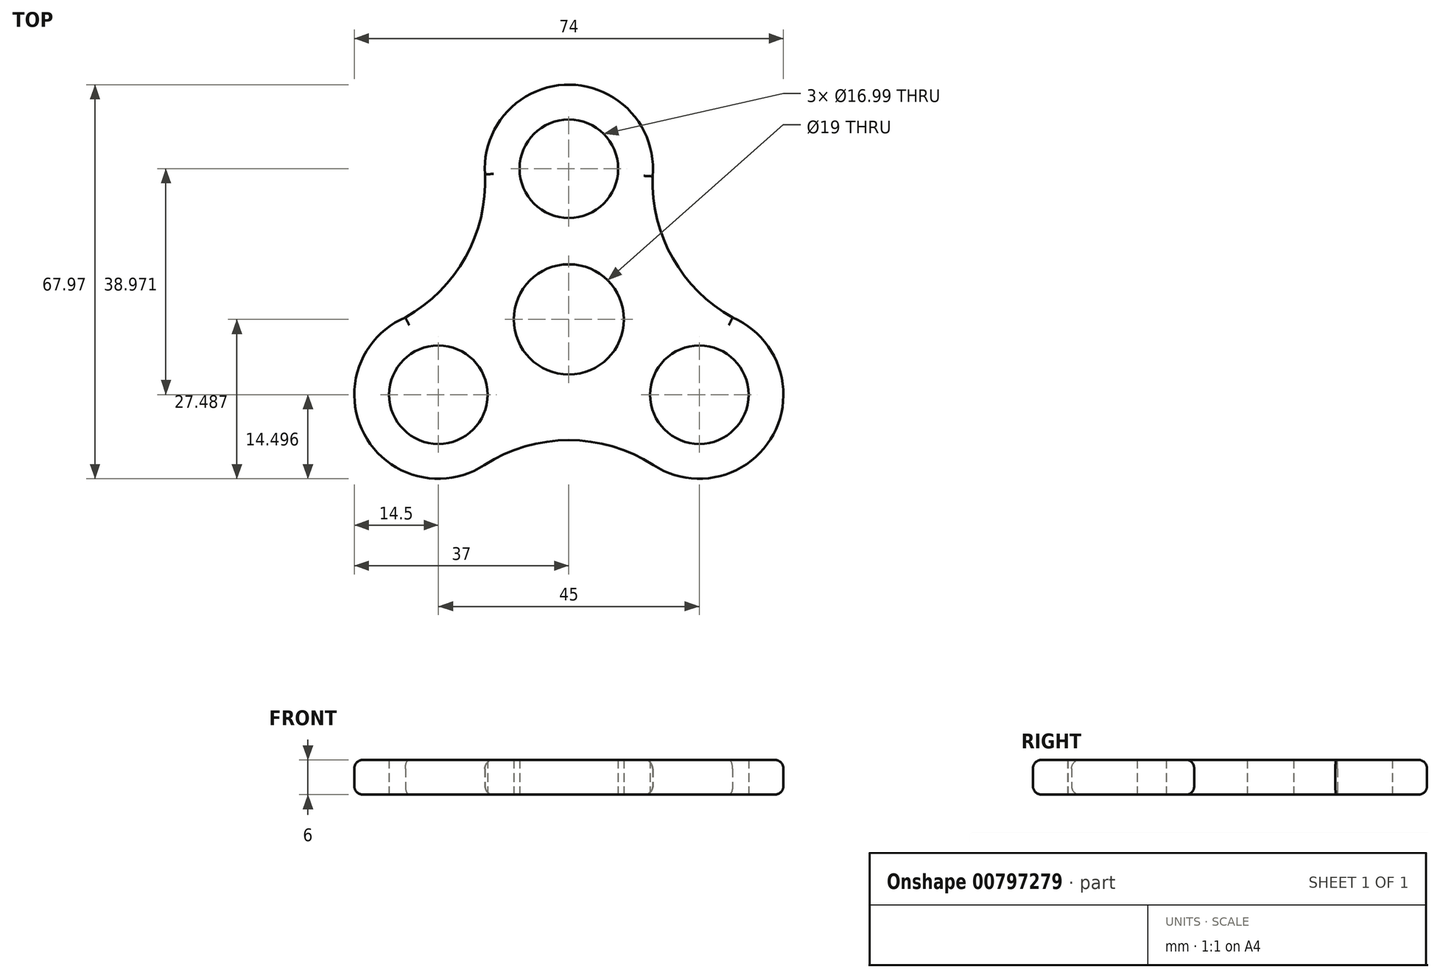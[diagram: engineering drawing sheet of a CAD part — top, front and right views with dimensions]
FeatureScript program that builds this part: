
annotation { "Feature Type Name" : "Feature", "Feature Type Description" : "" }
export const myFeature = defineFeature(function(context is Context, id is Id, definition is map)
    precondition{}
    {
        {
            var Q0;
            Q0=qCreatedBy(makeId("Top.planeOp"),FACE);
            var sketch = newSketch(context, id + "F0", { "sketchPlane" : qUnion([Q0])});
            skLineSegment(sketch, "E0", {"start": v(0, 26.77) * mm, "end": v(-22.5, -12.2) * mm, "construction": true});
            skLineSegment(sketch, "E1", {"start": v(-22.5, -12.2) * mm, "end": v(22.5, -12.2) * mm, "construction": true});
            skLineSegment(sketch, "E2", {"start": v(22.5, -12.2) * mm, "end": v(0, 26.77) * mm, "construction": true});
            skArc(sketch, "E3.0", {"start": v(-14.49, 26.16) * mm, "mid": v(-18.18, 10.92) * mm, "end": v(-29.75, 0.33) * mm});
            skArc(sketch, "E4.0", {"start": v(14.44, 25.45) * mm, "mid": v(0.17, 41.27) * mm, "end": v(-14.47, 25.8) * mm});
            skArc(sketch, "E5.0", {"start": v(28.46, 1) * mm, "mid": v(17.95, 11.3) * mm, "end": v(14.44, 25.6) * mm});
            skArc(sketch, "E6.0", {"start": v(14.57, -24.35) * mm, "mid": v(35.27, -19.06) * mm, "end": v(28.24, 1.1) * mm});
            skArc(sketch, "E7.0", {"start": v(-28.2, 1.13) * mm, "mid": v(-35.29, -19.04) * mm, "end": v(-14.57, -24.35) * mm});
            skArc(sketch, "E8.0", {"start": v(-14.64, -24.39) * mm, "mid": v(-0.03, -20.05) * mm, "end": v(14.58, -24.35) * mm});
            skLineSegment(sketch, "E9", {"start": v(-11.25, 7.28) * mm, "end": v(22.5, -12.2) * mm, "construction": true});
            skLineSegment(sketch, "E10", {"start": v(11.25, 7.28) * mm, "end": v(-22.5, -12.2) * mm, "construction": true});
            skLineSegment(sketch, "E11", {"start": v(0, -12.2) * mm, "end": v(0, 26.77) * mm, "construction": true});
            skCircle(sketch, "E12", {"center": v(22.5, -12.2) * mm, "radius": 8.5 * mm});
            skCircle(sketch, "E13", {"center": v(-22.5, -12.2) * mm, "radius": 8.5 * mm});
            skCircle(sketch, "E14", {"center": v(0, 26.77) * mm, "radius": 8.5 * mm});
            skCircle(sketch, "E15", {"center": v(0, 0.79) * mm, "radius": 9.5 * mm});
            skSolve(sketch);
        }
        {
            var Q0;
            Q0 = qSketchRegion(id + "F0", true);
            extrude(context, id + "F1", {"entities" : qUnion([Q0]), "depth" : 6 * mm, "offsetDistance" : 25.4 * mm});
        }
        {
            var Q0;
            Q0=makeQuery(id+"F1.opExtrude","CAP_EDGE",EDGE,{"disambiguationData":[OSD([sQuery(id+"F0.wireOp",EDGE,"E5.0")])],"isStart":false});
            var Q1;
            Q1=makeQuery(id+"F1.opExtrude","CAP_EDGE",EDGE,{"disambiguationData":[OSD([sQuery(id+"F0.wireOp",EDGE,"E3.0")])],"isStart":false});
            var Q2;
            Q2=makeQuery(id+"F1.opExtrude","CAP_EDGE",EDGE,{"disambiguationData":[OSD([sQuery(id+"F0.wireOp",EDGE,"E7.0")])],"isStart":false});
            var Q3;
            Q3=makeQuery(id+"F1.opExtrude","CAP_EDGE",EDGE,{"disambiguationData":[OSD([sQuery(id+"F0.wireOp",EDGE,"E6.0")])],"isStart":false});
            var Q4;
            Q4=makeQuery(id+"F1.opExtrude","CAP_EDGE",EDGE,{"disambiguationData":[OSD([sQuery(id+"F0.wireOp",EDGE,"E4.0")])],"isStart":false});
            var Q5;
            Q5=makeQuery(id+"F1.opExtrude","CAP_EDGE",EDGE,{"disambiguationData":[OSD([sQuery(id+"F0.wireOp",EDGE,"E8.0")])],"isStart":true});
            var Q6;
            Q6=makeQuery(id+"F1.opExtrude","CAP_EDGE",EDGE,{"disambiguationData":[OSD([sQuery(id+"F0.wireOp",EDGE,"E6.0")])],"isStart":true});
            var Q7;
            Q7=makeQuery(id+"F1.opExtrude","CAP_EDGE",EDGE,{"disambiguationData":[OSD([sQuery(id+"F0.wireOp",EDGE,"E7.0")])],"isStart":true});
            var Q8;
            Q8=makeQuery(id+"F1.opExtrude","CAP_EDGE",EDGE,{"disambiguationData":[OSD([sQuery(id+"F0.wireOp",EDGE,"E5.0")])],"isStart":true});
            var Q9;
            Q9=makeQuery(id+"F1.opExtrude","CAP_EDGE",EDGE,{"disambiguationData":[OSD([sQuery(id+"F0.wireOp",EDGE,"E3.0")])],"isStart":true});
            var Q10;
            Q10=makeQuery(id+"F1.opExtrude","CAP_EDGE",EDGE,{"disambiguationData":[OSD([sQuery(id+"F0.wireOp",EDGE,"E4.0")])],"isStart":true});
            fillet(context, id + "F2", {"entities" : qUnion([Q0, Q1, Q2, Q3, Q4, Q5, Q6, Q7, Q8, Q9, Q10]), "radius" : 1.5 * mm, "tangentPropagation" : true, "allowEdgeOverflow" : false});
        }
    });
